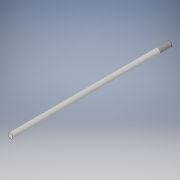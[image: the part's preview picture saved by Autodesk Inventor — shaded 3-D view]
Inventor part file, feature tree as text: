
AUTODESK INVENTOR PART (.ipt)
format: ipt  version: 2018 (Build 220112000, 112)  size: 93,696 bytes
history: native  units: in
note: dims shown in document units (in); Inventor stores cm internally (conversion verified against a paired STEP export)
features: extrude x1, thread x1, sketch x1
ambient origin geometry x8: Origin, YZ Plane, XZ Plane, XY Plane, X Axis, Y Axis, Z Axis, Center Point
bodies: Solid1 (feature_tree)
feature tree (3):
  extrude  "Extrusion1"  Depth=8.0in TaperAngle=0.0deg
  thread  "Thread1"  [1 undecoded]
  sketch  "Sketch1"  dims[d0=0.25in d1=8.0in d2=0.0in d3=0.6in d4=7.4in]
note: 1 required parameter value undecoded (feature->parameter linkage not recoverable at this tier; creation-order binding heuristic only, values carry confidence <= 0.55)
